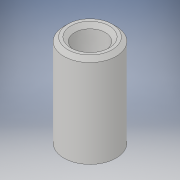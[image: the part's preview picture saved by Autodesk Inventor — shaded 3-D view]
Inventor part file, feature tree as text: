
AUTODESK INVENTOR PART (.ipt)
format: ipt  version: 2018 (Build 220112000, 112)  size: 107,008 bytes
history: native  units: in
note: dims shown in document units (in); Inventor stores cm internally (conversion verified against a paired STEP export)
features: extrude x1, chamfer x1, sketch x1
ambient origin geometry x8: Origin, YZ Plane, XZ Plane, XY Plane, X Axis, Y Axis, Z Axis, Center Point
bodies: Solid1 (feature_tree)
feature tree (3):
  extrude  "Extrusion1"  Depth=0.125in
  chamfer  "Chamfer1"  Distance=0.75in
  sketch  "Sketch1"  dims[d0=0.25in d1=0.425in d2=0.75in d3=0.0in d4=0.0312in d5=0.125in d6=45.0deg]
